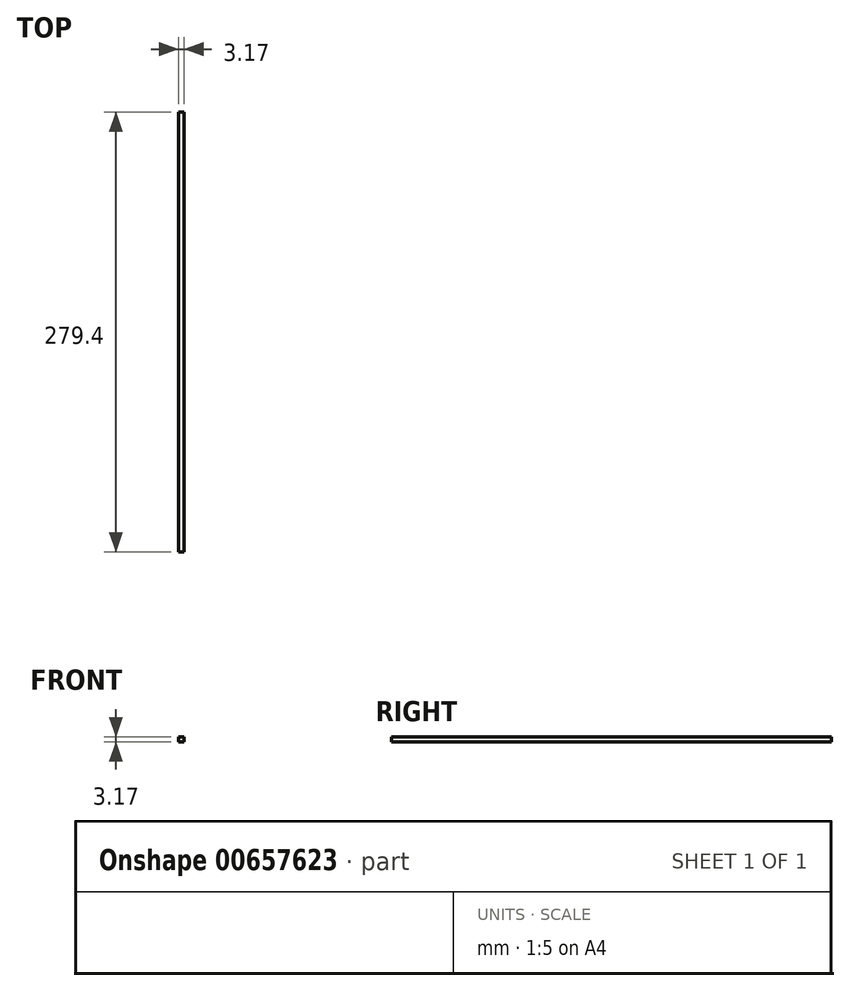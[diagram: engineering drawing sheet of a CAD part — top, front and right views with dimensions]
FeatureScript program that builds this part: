
annotation { "Feature Type Name" : "Feature", "Feature Type Description" : "" }
export const myFeature = defineFeature(function(context is Context, id is Id, definition is map)
    precondition{}
    {
        {
            var Q0;
            Q0=qCreatedBy(makeId("Front.planeOp"),FACE);
            var sketch = newSketch(context, id + "F0", { "sketchPlane" : qUnion([Q0])});
            skLineSegment(sketch, "E0.bottom", {"start": v(0, 0) * mm, "end": v(3.18, 0) * mm});
            skLineSegment(sketch, "E0.top", {"start": v(0, -3.18) * mm, "end": v(3.18, -3.18) * mm});
            skLineSegment(sketch, "E0.left", {"start": v(0, 0) * mm, "end": v(0, -3.18) * mm});
            skLineSegment(sketch, "E0.right", {"start": v(3.18, 0) * mm, "end": v(3.18, -3.18) * mm});
            skSolve(sketch);
        }
        {
            var Q0;
            Q0=makeQuery(id+"F0.imprint","IMPRINT",FACE,{"disambiguationData":[TD([[makeQuery(id+"F0.imprint","IMPRINT",EDGE,{"derivedFrom":sQuery(id+"F0.wireOp",EDGE,"E0.bottom")}),-1.0]])]});
            extrude(context, id + "F1", {"entities" : qUnion([Q0]), "depth" : 279.4 * mm, "offsetDistance" : 25.4 * mm});
        }
    });
